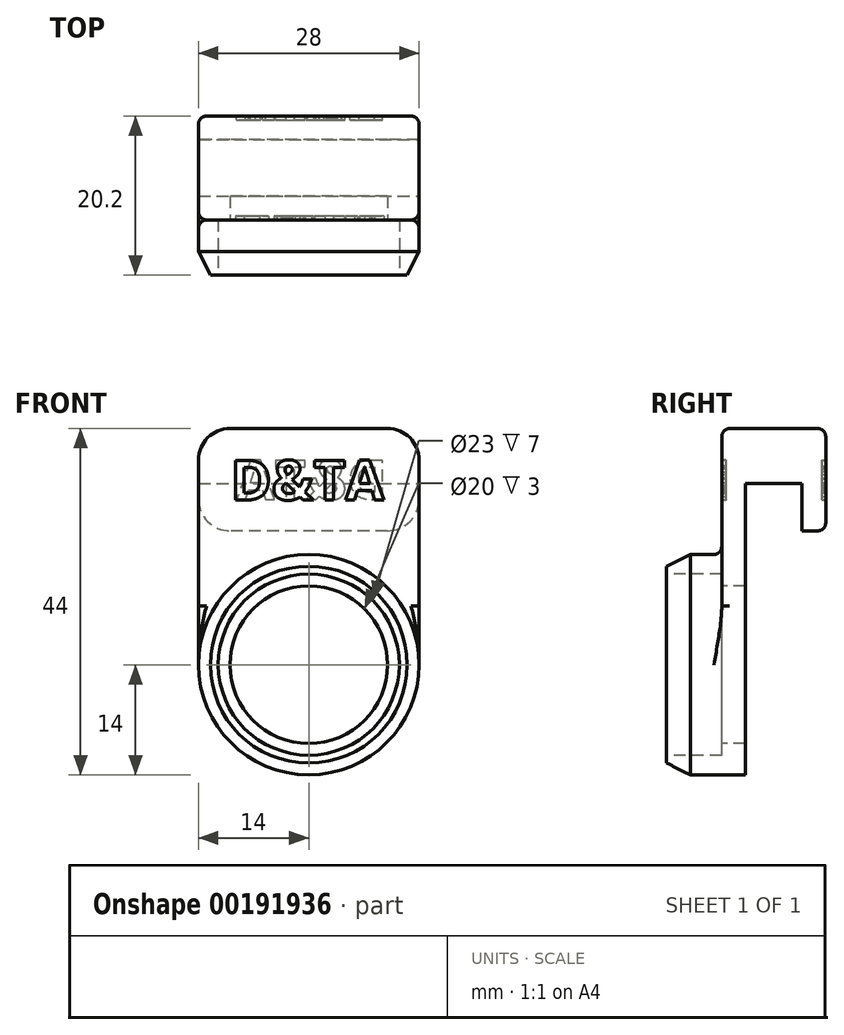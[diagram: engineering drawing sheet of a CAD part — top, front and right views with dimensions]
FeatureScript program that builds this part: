
annotation { "Feature Type Name" : "Feature", "Feature Type Description" : "" }
export const myFeature = defineFeature(function(context is Context, id is Id, definition is map)
    precondition{}
    {
        {
            var Q0;
            Q0=qCreatedBy(makeId("Front.planeOp"),FACE);
            var sketch = newSketch(context, id + "F0", { "sketchPlane" : qUnion([Q0])});
            skCircle(sketch, "E0", {"center": v(0, 0) * mm, "radius": 14 * mm});
            skSolve(sketch);
        }
        {
            var Q0;
            Q0 = qSketchRegion(id + "F0", true);
            extrude(context, id + "F1", {"entities" : qUnion([Q0]), "depth" : 10 * mm});
        }
        {
            var Q0;
            Q0=qCreatedBy(makeId("Front.planeOp"),FACE);
            var sketch = newSketch(context, id + "F2", { "sketchPlane" : qUnion([Q0])});
            skLineSegment(sketch, "E1.bottom", {"start": v(-14, 30) * mm, "end": v(14, 30) * mm});
            skLineSegment(sketch, "E1.top", {"start": v(-14, 23) * mm, "end": v(14, 23) * mm});
            skLineSegment(sketch, "E1.left", {"start": v(-14, 30) * mm, "end": v(-14, 23) * mm});
            skLineSegment(sketch, "E1.right", {"start": v(14, 30) * mm, "end": v(14, 23) * mm});
            skPoint(sketch, "E1.middle", {"position": v(0, 26.5) * mm});
            skSolve(sketch);
        }
        {
            var Q0;
            Q0=makeQuery(id+"F2.imprint","IMPRINT",FACE,{"disambiguationData":[TD([[makeQuery(id+"F2.imprint","IMPRINT",EDGE,{"derivedFrom":sQuery(id+"F2.wireOp",EDGE,"E1.bottom")}),-1.0]])]});
            extrude(context, id + "F3", {"entities" : qUnion([Q0]), "oppositeDirection" : true, "depth" : 7.2 * mm});
        }
        {
            var Q0;
            Q0=qCreatedBy(makeId("Front.planeOp"),FACE);
            var sketch = newSketch(context, id + "F4", { "sketchPlane" : qUnion([Q0])});
            skLineSegment(sketch, "E2.bottom", {"start": v(-14, 30) * mm, "end": v(14, 30) * mm});
            skLineSegment(sketch, "E2.left", {"start": v(-14, 30) * mm, "end": v(-14, 0) * mm});
            skLineSegment(sketch, "E2.right", {"start": v(14, 30) * mm, "end": v(14, 0) * mm});
            skArc(sketch, "E3", {"start": v(-14, 0) * mm, "mid": v(0, -14) * mm, "end": v(14, 0) * mm});
            skSolve(sketch);
        }
        {
            var Q0;
            Q0=makeQuery(id+"F4.imprint","IMPRINT",FACE,{"disambiguationData":[TD([[makeQuery(id+"F4.imprint","IMPRINT",EDGE,{"derivedFrom":sQuery(id+"F4.wireOp",EDGE,"E2.bottom")}),-1.0]])]});
            extrude(context, id + "F5", {"entities" : qUnion([Q0]), "depth" : 3 * mm});
        }
        {
            var Q0;
            Q0=makeQuery(id+"F3.opExtrude","CAP_FACE",FACE,{"disambiguationData":[OSD([sQuery(id+"F2.wireOp",EDGE,"E1.bottom"),sQuery(id+"F2.wireOp",EDGE,"E1.top"),sQuery(id+"F2.wireOp",EDGE,"E1.left"),sQuery(id+"F2.wireOp",EDGE,"E1.right")])],"isStart":false});
            var sketch = newSketch(context, id + "F6", { "sketchPlane" : qUnion([Q0])});
            skLineSegment(sketch, "E4.bottom", {"start": v(-14, 30) * mm, "end": v(14, 30) * mm});
            skLineSegment(sketch, "E4.top", {"start": v(-14, 17) * mm, "end": v(14, 17) * mm});
            skLineSegment(sketch, "E4.left", {"start": v(-14, 30) * mm, "end": v(-14, 17) * mm});
            skLineSegment(sketch, "E4.right", {"start": v(14, 30) * mm, "end": v(14, 17) * mm});
            skSolve(sketch);
        }
        {
            var Q0;
            {var subQ0=sQuery(id+"F6.wireOp",EDGE,"E4.top");Q0=makeQuery(id+"F6.imprint","IMPRINT",FACE,{"disambiguationData":[TD([[makeQuery(id+"F6.imprint","IMPRINT",EDGE,{"derivedFrom":subQ0}),1.0]])]});}
            var Q1;
            {var subQ0=sQuery(id+"F6.wireOp",EDGE,"E4.bottom");Q1=makeQuery(id+"F6.imprint","IMPRINT",FACE,{"disambiguationData":[TD([[makeQuery(id+"F6.imprint","IMPRINT",EDGE,{"derivedFrom":subQ0}),1.0]])]});}
            extrude(context, id + "F7", {"entities" : qUnion([Q0, Q1]), "operationType" : NewBodyOperationType.ADD, "depth" : 3 * mm});
        }
        {
            var Q0;
            Q0=makeQuery(id+"F7.boolean.opBoolean","MERGE",EDGE,{"derivedFrom":[makeQuery(id+"F3.opExtrude","SWEPT_EDGE",EDGE,{"disambiguationData":[OSD([sQuery(id+"F2.wireOp",EDGE,"E1.bottom"),sQuery(id+"F2.wireOp",EDGE,"E1.right")])]}),makeQuery(id+"F7.opExtrude","SWEPT_EDGE",EDGE,{"disambiguationData":[OSD([sQuery(id+"F6.wireOp",EDGE,"E4.bottom"),sQuery(id+"F6.wireOp",EDGE,"E4.left")])]})]});
            var Q1;
            Q1=makeQuery(id+"F7.boolean.opBoolean","MERGE",EDGE,{"derivedFrom":[makeQuery(id+"F3.opExtrude","SWEPT_EDGE",EDGE,{"disambiguationData":[OSD([sQuery(id+"F2.wireOp",EDGE,"E1.bottom"),sQuery(id+"F2.wireOp",EDGE,"E1.left")])]}),makeQuery(id+"F7.opExtrude","SWEPT_EDGE",EDGE,{"disambiguationData":[OSD([sQuery(id+"F6.wireOp",EDGE,"E4.bottom"),sQuery(id+"F6.wireOp",EDGE,"E4.right")])]})]});
            var Q2;
            Q2=makeQuery(id+"F7.opExtrude","SWEPT_EDGE",EDGE,{"disambiguationData":[OSD([sQuery(id+"F6.wireOp",EDGE,"E4.top"),sQuery(id+"F6.wireOp",EDGE,"E4.left")])]});
            var Q3;
            Q3=makeQuery(id+"F7.opExtrude","SWEPT_EDGE",EDGE,{"disambiguationData":[OSD([sQuery(id+"F6.wireOp",EDGE,"E4.top"),sQuery(id+"F6.wireOp",EDGE,"E4.right")])]});
            fillet(context, id + "F8", {"entities" : qUnion([Q0, Q1, Q2, Q3]), "radius" : 4 * mm, "tangentPropagation" : true, "allowEdgeOverflow" : false});
        }
        {
            var Q0;
            Q0=makeQuery(id+"F1.opExtrude","SWEPT_BODY",BODY,{"disambiguationData":[OSD([sQuery(id+"F0.wireOp",EDGE,"E0")])]});
            var Q1;
            Q1=makeQuery(id+"F5.opExtrude","SWEPT_BODY",BODY,{"disambiguationData":[OSD([sQuery(id+"F4.wireOp",EDGE,"E2.bottom"),sQuery(id+"F4.wireOp",EDGE,"E2.left"),sQuery(id+"F4.wireOp",EDGE,"E2.right"),sQuery(id+"F4.wireOp",EDGE,"E3")])]});
            var Q2;
            Q2=makeQuery(id+"F3.opExtrude","SWEPT_BODY",BODY,{"disambiguationData":[OSD([sQuery(id+"F2.wireOp",EDGE,"E1.bottom"),sQuery(id+"F2.wireOp",EDGE,"E1.top"),sQuery(id+"F2.wireOp",EDGE,"E1.left"),sQuery(id+"F2.wireOp",EDGE,"E1.right")])]});
            booleanBodies(context, id + "F9", {"operationType" : BooleanOperationType.UNION, "tools" : qUnion([Q0, Q1, Q2])});
        }
        {
            var Q0;
            Q0=makeQuery(id+"F9.opBoolean","INTERSECT",EDGE,{"derivedFrom":[makeQuery(id+"F1.opExtrude","SWEPT_FACE",FACE,{"disambiguationData":[OSD([sQuery(id+"F0.wireOp",EDGE,"E0")])]}),makeQuery(id+"F5.opExtrude","CAP_FACE",FACE,{"disambiguationData":[OSD([sQuery(id+"F4.wireOp",EDGE,"E2.bottom"),sQuery(id+"F4.wireOp",EDGE,"E2.left"),sQuery(id+"F4.wireOp",EDGE,"E2.right"),sQuery(id+"F4.wireOp",EDGE,"E3")])],"isStart":false})]});
            fillet(context, id + "F10", {"entities" : qUnion([Q0]), "radius" : 1 * mm, "tangentPropagation" : true, "allowEdgeOverflow" : false});
        }
        {
            var Q0;
            Q0=makeQuery(id+"F5.opExtrude","SWEPT_EDGE",EDGE,{"disambiguationData":[OSD([sQuery(id+"F4.wireOp",EDGE,"E2.bottom"),sQuery(id+"F4.wireOp",EDGE,"E2.left")])]});
            var Q1;
            Q1=makeQuery(id+"F5.opExtrude","SWEPT_EDGE",EDGE,{"disambiguationData":[OSD([sQuery(id+"F4.wireOp",EDGE,"E2.bottom"),sQuery(id+"F4.wireOp",EDGE,"E2.right")])]});
            fillet(context, id + "F11", {"entities" : qUnion([Q0, Q1]), "radius" : 4 * mm, "tangentPropagation" : true, "allowEdgeOverflow" : false});
        }
        {
            var Q0;
            Q0=makeQuery(id+"F5.opExtrude","CAP_EDGE",EDGE,{"disambiguationData":[OSD([sQuery(id+"F4.wireOp",EDGE,"E2.left")])],"isStart":false});
            var Q1;
            Q1=makeQuery(id+"F7.opExtrude","CAP_EDGE",EDGE,{"disambiguationData":[OSD([sQuery(id+"F6.wireOp",EDGE,"E4.right")])],"isStart":false});
            fillet(context, id + "F12", {"entities" : qUnion([Q0, Q1]), "radius" : 1 * mm, "tangentPropagation" : true, "allowEdgeOverflow" : false});
        }
        {
            var Q0;
            Q0=makeQuery(id+"F1.opExtrude","CAP_FACE",FACE,{"disambiguationData":[OSD([sQuery(id+"F0.wireOp",EDGE,"E0")])],"isStart":false});
            var sketch = newSketch(context, id + "F13", { "sketchPlane" : qUnion([Q0])});
            skCircle(sketch, "E5", {"center": v(0, 0) * mm, "radius": 11.5 * mm});
            skSolve(sketch);
        }
        {
            var Q0;
            Q0=makeQuery(id+"F13.imprint","IMPRINT",FACE,{"disambiguationData":[TD([[makeQuery(id+"F13.imprint","IMPRINT",EDGE,{"derivedFrom":sQuery(id+"F13.wireOp",EDGE,"E5")}),1.0]])]});
            extrude(context, id + "F14", {"entities" : qUnion([Q0]), "operationType" : NewBodyOperationType.REMOVE, "oppositeDirection" : true, "depth" : 7 * mm});
        }
        {
            var Q0;
            Q0=makeQuery(id+"F14.boolean.opBoolean","COPY",FACE,{"derivedFrom":makeQuery(id+"F14.opExtrude","CAP_FACE",FACE,{"disambiguationData":[OSD([sQuery(id+"F13.wireOp",EDGE,"E5")])],"isStart":false})});
            var sketch = newSketch(context, id + "F15", { "sketchPlane" : qUnion([Q0])});
            skCircle(sketch, "E6", {"center": v(0, 0) * mm, "radius": 10 * mm});
            skSolve(sketch);
        }
        {
            var Q0;
            Q0=makeQuery(id+"F15.imprint","IMPRINT",FACE,{"disambiguationData":[TD([[makeQuery(id+"F15.imprint","IMPRINT",EDGE,{"derivedFrom":sQuery(id+"F15.wireOp",EDGE,"E6")}),1.0]])]});
            extrude(context, id + "F16", {"entities" : qUnion([Q0]), "operationType" : NewBodyOperationType.REMOVE, "endBound" : BoundingType.UP_TO_NEXT, "oppositeDirection" : true, "depth" : 25 * mm});
        }
        {
            var Q0;
            Q0=makeQuery(id+"F1.opExtrude","CAP_EDGE",EDGE,{"disambiguationData":[OSD([sQuery(id+"F0.wireOp",EDGE,"E0")])],"isStart":false});
            chamfer(context, id + "F17", {"entities" : qUnion([Q0]), "chamferType" : ChamferType.TWO_OFFSETS, "width1" : 1.5 * mm, "oppositeDirection" : false, "width2" : 3 * mm, "tangentPropagation" : true});
        }
        {
            var Q0;
            Q0=makeQuery(id+"F5.opExtrude","CAP_FACE",FACE,{"disambiguationData":[OSD([sQuery(id+"F4.wireOp",EDGE,"E2.bottom"),sQuery(id+"F4.wireOp",EDGE,"E2.left"),sQuery(id+"F4.wireOp",EDGE,"E2.right"),sQuery(id+"F4.wireOp",EDGE,"E3")])],"isStart":false});
            var sketch = newSketch(context, id + "F18", { "sketchPlane" : qUnion([Q0])});
            skText(sketch, "E7", { "text": "D&TA", "fontName": "OpenSans-Bold.ttf"});
            const initialGuessF18  = {"E7": [-0.00994, 0.02092, 1, 0, 0.00508]};
            skSetInitialGuess(sketch, initialGuessF18);
            skSolve(sketch);
        }
        {
            var Q0;
            Q0 = qSketchRegion(id + "F18", true);
            extrude(context, id + "F19", {"entities" : qUnion([Q0]), "operationType" : NewBodyOperationType.REMOVE, "oppositeDirection" : true, "depth" : 0.5 * mm});
        }
        {
            var Q0;
            Q0=makeQuery(id+"F7.opExtrude","CAP_FACE",FACE,{"disambiguationData":[OSD([sQuery(id+"F6.wireOp",EDGE,"E4.bottom"),sQuery(id+"F6.wireOp",EDGE,"E4.top"),sQuery(id+"F6.wireOp",EDGE,"E4.left"),sQuery(id+"F6.wireOp",EDGE,"E4.right")])],"isStart":false});
            var sketch = newSketch(context, id + "F20", { "sketchPlane" : qUnion([Q0])});
            skText(sketch, "E8", { "text": "D&TA", "fontName": "OpenSans-Bold.ttf"});
            const initialGuessF20  = {"E8": [-0.01, 0.021, 1, 0, 0.005]};
            skSetInitialGuess(sketch, initialGuessF20);
            skSolve(sketch);
        }
        {
            var Q0;
            Q0 = qSketchRegion(id + "F20", true);
            extrude(context, id + "F21", {"entities" : qUnion([Q0]), "operationType" : NewBodyOperationType.REMOVE, "oppositeDirection" : true, "depth" : 0.5 * mm});
        }
    });
